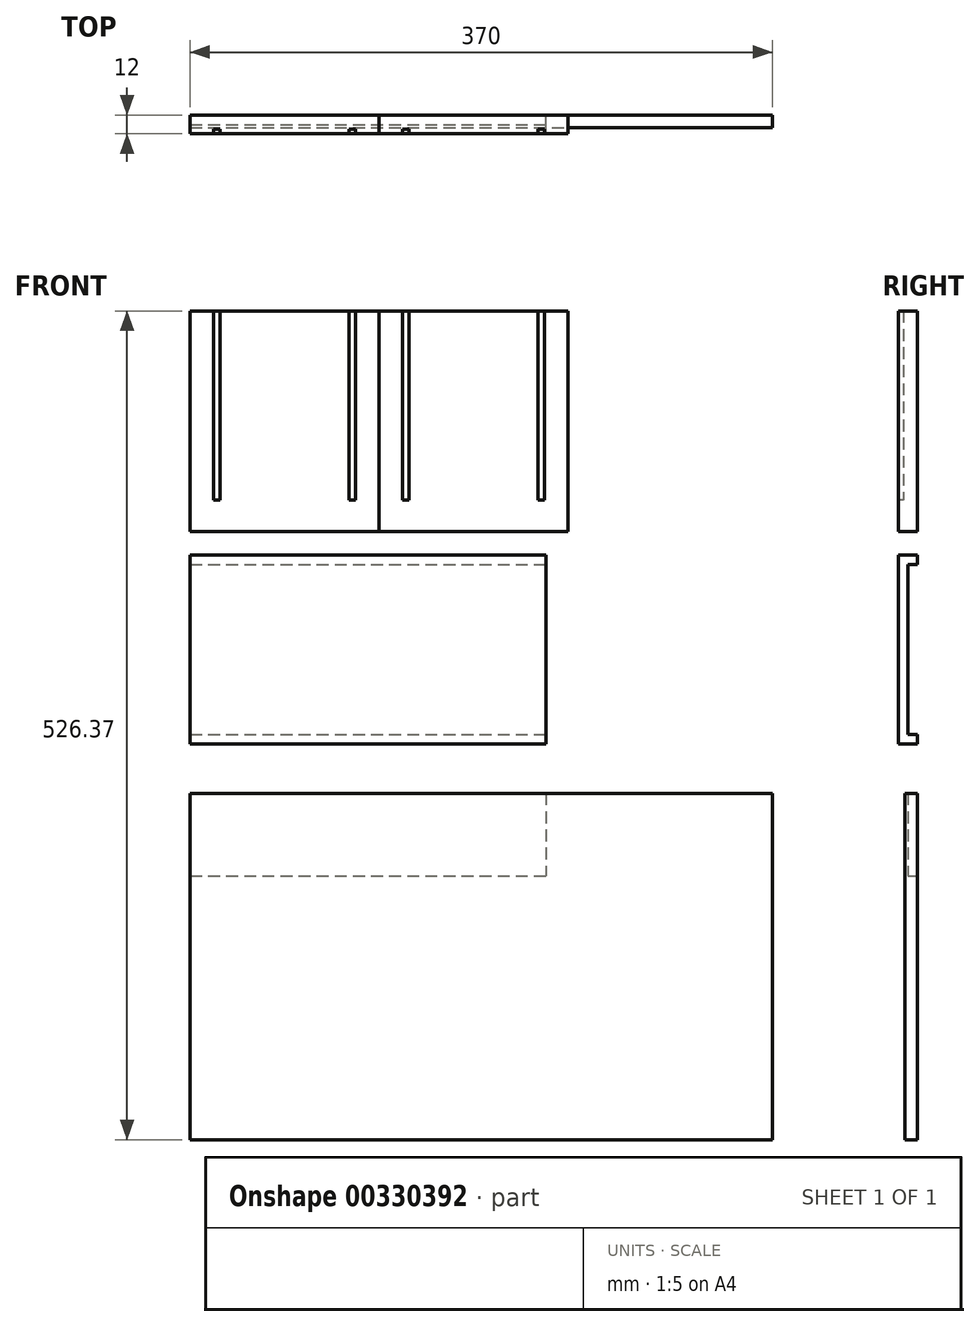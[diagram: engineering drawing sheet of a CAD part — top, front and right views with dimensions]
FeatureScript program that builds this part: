
annotation { "Feature Type Name" : "Feature", "Feature Type Description" : "" }
export const myFeature = defineFeature(function(context is Context, id is Id, definition is map)
    precondition{}
    {
        {
            var Q0;
            Q0=qCreatedBy(makeId("Front.planeOp"),FACE);
            var sketch = newSketch(context, id + "F0", { "sketchPlane" : qUnion([Q0])});
            skLineSegment(sketch, "E0.bottom", {"start": v(0, 0) * mm, "end": v(120, 0) * mm});
            skLineSegment(sketch, "E0.top", {"start": v(0, 140) * mm, "end": v(120, 140) * mm});
            skLineSegment(sketch, "E0.left", {"start": v(0, 0) * mm, "end": v(0, 140) * mm});
            skLineSegment(sketch, "E0.right", {"start": v(120, 0) * mm, "end": v(120, 140) * mm});
            skSolve(sketch);
        }
        {
            var Q0;
            Q0 = qSketchRegion(id + "F0", true);
            extrude(context, id + "F1", {"entities" : qUnion([Q0]), "depth" : 12 * mm});
        }
        {
            var Q0;
            Q0=makeQuery(id+"F1.opExtrude","CAP_FACE",FACE,{"disambiguationData":[OSD([sQuery(id+"F0.wireOp",EDGE,"E0.bottom"),sQuery(id+"F0.wireOp",EDGE,"E0.top"),sQuery(id+"F0.wireOp",EDGE,"E0.left"),sQuery(id+"F0.wireOp",EDGE,"E0.right")])],"isStart":false});
            cPlane(context, id + "F2", {"entities" : qUnion([Q0]), "cplaneType" : CPlaneType.OFFSET, "offset" : 0 * mm, "width" : 150 * mm, "height" : 150 * mm});
        }
        {
            var Q0;
            Q0=qCreatedBy(id+"F2.planeOp",FACE);
            var sketch = newSketch(context, id + "F3", { "sketchPlane" : qUnion([Q0])});
            skLineSegment(sketch, "E1.bottom", {"start": v(15, 140) * mm, "end": v(19, 140) * mm});
            skLineSegment(sketch, "E1.top", {"start": v(15, 20) * mm, "end": v(19, 20) * mm});
            skLineSegment(sketch, "E1.left", {"start": v(15, 140) * mm, "end": v(15, 20) * mm});
            skLineSegment(sketch, "E1.right", {"start": v(19, 140) * mm, "end": v(19, 20) * mm});
            skSolve(sketch);
        }
        {
            var Q0;
            Q0 = qSketchRegion(id + "F3", true);
            extrude(context, id + "F4", {"entities" : qUnion([Q0]), "operationType" : NewBodyOperationType.REMOVE, "oppositeDirection" : true, "depth" : 3 * mm});
        }
        {
            var Q0;
            Q0=qCreatedBy(id+"F2.planeOp",FACE);
            var sketch = newSketch(context, id + "F5", { "sketchPlane" : qUnion([Q0])});
            skLineSegment(sketch, "E2.bottom", {"start": v(101, 140) * mm, "end": v(105, 140) * mm});
            skLineSegment(sketch, "E2.top", {"start": v(101, 20) * mm, "end": v(105, 20) * mm});
            skLineSegment(sketch, "E2.left", {"start": v(101, 140) * mm, "end": v(101, 20) * mm});
            skLineSegment(sketch, "E2.right", {"start": v(105, 140) * mm, "end": v(105, 20) * mm});
            skSolve(sketch);
        }
        {
            var Q0;
            Q0 = qSketchRegion(id + "F5", true);
            extrude(context, id + "F6", {"entities" : qUnion([Q0]), "operationType" : NewBodyOperationType.REMOVE, "oppositeDirection" : true, "depth" : 3 * mm});
        }
        {
            var Q0;
            Q0=makeQuery(id+"F1.opExtrude","SWEPT_BODY",BODY,{"disambiguationData":[OSD([sQuery(id+"F0.wireOp",EDGE,"E0.bottom"),sQuery(id+"F0.wireOp",EDGE,"E0.top"),sQuery(id+"F0.wireOp",EDGE,"E0.left"),sQuery(id+"F0.wireOp",EDGE,"E0.right")])]});
            transform(context, id + "F7", {"entities" : qUnion([Q0]), "transformType" : TransformType.TRANSLATION_3D, "dx" : 120 * mm, "dy" : 0 * mm, "dz" : 0 * mm, "makeCopy" : true});
        }
        {
            var Q0;
            Q0=qCreatedBy(makeId("Front.planeOp"),FACE);
            var sketch = newSketch(context, id + "F8", { "sketchPlane" : qUnion([Q0])});
            skLineSegment(sketch, "E3.bottom", {"start": v(0, -14.9) * mm, "end": v(226, -14.9) * mm});
            skLineSegment(sketch, "E3.top", {"start": v(0, -134.9) * mm, "end": v(226, -134.9) * mm});
            skLineSegment(sketch, "E3.left", {"start": v(0, -14.9) * mm, "end": v(0, -134.9) * mm});
            skLineSegment(sketch, "E3.right", {"start": v(226, -14.9) * mm, "end": v(226, -134.9) * mm});
            skLineSegment(sketch, "E4", {"start": v(-11.06, -20.9) * mm, "end": v(240.96, -20.9) * mm, "construction": true});
            skLineSegment(sketch, "E5", {"start": v(-10.2, -128.9) * mm, "end": v(234.93, -128.9) * mm, "construction": true});
            skLineSegment(sketch, "E6.bottom", {"start": v(0, -20.9) * mm, "end": v(226, -20.9) * mm});
            skLineSegment(sketch, "E6.top", {"start": v(0, -128.9) * mm, "end": v(226, -128.9) * mm});
            skLineSegment(sketch, "E6.left", {"start": v(0, -20.9) * mm, "end": v(0, -128.9) * mm});
            skLineSegment(sketch, "E6.right", {"start": v(226, -20.9) * mm, "end": v(226, -128.9) * mm});
            skSolve(sketch);
        }
        {
            var Q0;
            {var subQ0=sQuery(id+"F8.wireOp",EDGE,"E3.bottom");Q0=makeQuery(id+"F8.imprint","IMPRINT",FACE,{"disambiguationData":[TD([[makeQuery(id+"F8.imprint","IMPRINT",EDGE,{"derivedFrom":subQ0}),-1.0]])]});}
            var Q1;
            Q1=makeQuery(id+"F8.imprint","IMPRINT",FACE,{"disambiguationData":[TD([[makeQuery(id+"F8.imprint","IMPRINT",EDGE,{"derivedFrom":sQuery(id+"F8.wireOp",EDGE,"E6.bottom")}),-1.0]])]});
            var Q2;
            {var subQ0=sQuery(id+"F8.wireOp",EDGE,"E3.top");Q2=makeQuery(id+"F8.imprint","IMPRINT",FACE,{"disambiguationData":[TD([[makeQuery(id+"F8.imprint","IMPRINT",EDGE,{"derivedFrom":subQ0}),1.0]])]});}
            extrude(context, id + "F9", {"entities" : qUnion([Q0, Q1, Q2]), "depth" : 12 * mm});
        }
        {
            var Q0;
            Q0=qCreatedBy(makeId("Front.planeOp"),FACE);
            var sketch = newSketch(context, id + "F10", { "sketchPlane" : qUnion([Q0])});
            skLineSegment(sketch, "E7.bottom", {"start": v(0, -363.37) * mm, "end": v(370, -363.37) * mm});
            skLineSegment(sketch, "E7.top", {"start": v(0, -583.37) * mm, "end": v(370, -583.37) * mm});
            skLineSegment(sketch, "E7.left", {"start": v(0, -363.37) * mm, "end": v(0, -583.37) * mm});
            skLineSegment(sketch, "E7.right", {"start": v(370, -363.37) * mm, "end": v(370, -583.37) * mm});
            skSolve(sketch);
        }
        {
            var Q0;
            Q0 = qSketchRegion(id + "F10", true);
            extrude(context, id + "F11", {"entities" : qUnion([Q0]), "depth" : 8 * mm});
        }
        {
            var Q0;
            Q0=makeQuery(id+"F11.opExtrude","SWEPT_BODY",BODY,{"disambiguationData":[OSD([sQuery(id+"F10.wireOp",EDGE,"E7.bottom"),sQuery(id+"F10.wireOp",EDGE,"E7.top"),sQuery(id+"F10.wireOp",EDGE,"E7.left"),sQuery(id+"F10.wireOp",EDGE,"E7.right")])]});
            transform(context, id + "F12", {"entities" : qUnion([Q0]), "transformType" : TransformType.TRANSLATION_3D, "dx" : 0 * mm, "dy" : 0 * mm, "dz" : 287 * mm, "makeCopy" : false});
        }
        {
            var Q0;
            Q0=makeQuery(id+"F8.imprint","IMPRINT",FACE,{"disambiguationData":[TD([[makeQuery(id+"F8.imprint","IMPRINT",EDGE,{"derivedFrom":sQuery(id+"F8.wireOp",EDGE,"E6.bottom")}),-1.0]])]});
            extrude(context, id + "F13", {"entities" : qUnion([Q0]), "operationType" : NewBodyOperationType.REMOVE, "depth" : 6 * mm});
        }
        {
            var Q0;
            Q0=makeQuery(id+"F11.opExtrude","SWEPT_BODY",BODY,{"disambiguationData":[OSD([sQuery(id+"F10.wireOp",EDGE,"E7.bottom"),sQuery(id+"F10.wireOp",EDGE,"E7.top"),sQuery(id+"F10.wireOp",EDGE,"E7.left"),sQuery(id+"F10.wireOp",EDGE,"E7.right")])]});
            transform(context, id + "F14", {"entities" : qUnion([Q0]), "transformType" : TransformType.TRANSLATION_3D, "dx" : 0 * mm, "dy" : 0 * mm, "dz" : -90 * mm, "makeCopy" : false});
        }
    });
